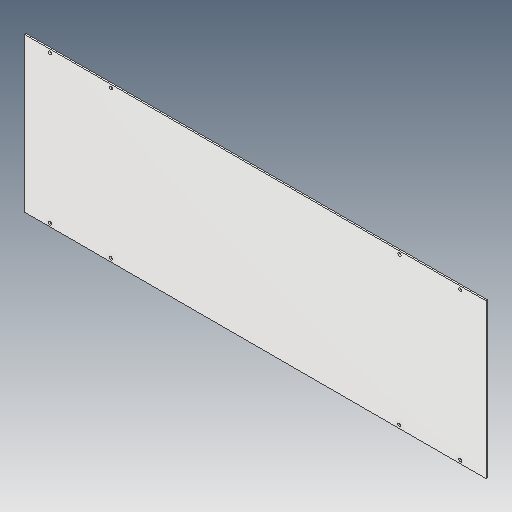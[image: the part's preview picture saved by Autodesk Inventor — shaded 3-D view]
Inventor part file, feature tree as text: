
AUTODESK INVENTOR PART (.ipt)
format: ipt  version: 2023.5 (Build 275446000, 446)  size: 91,648 bytes
history: native  units: in
note: dims shown in document units (in); Inventor stores cm internally (conversion verified against a paired STEP export)
features: mirror x1
ambient origin geometry x8: Origin, YZ Plane, XZ Plane, XY Plane, X Axis, Y Axis, Z Axis, Center Point
bodies: Solid1 (feature_tree)
feature tree (1):
  mirror  "Mirror1"
